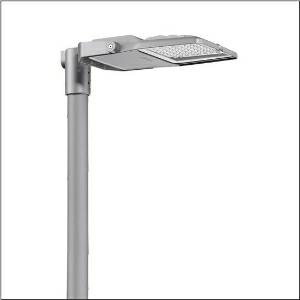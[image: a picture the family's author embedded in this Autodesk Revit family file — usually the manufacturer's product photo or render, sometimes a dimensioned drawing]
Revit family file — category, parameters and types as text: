
# Revit family: floodlight_fl_21_mini___pl61_5xa7776c2c3a_9e20
name_source: partatom
category: Lighting Fixtures
units: mm (PartAtom-declared; Revit-internal decimal feet)

## family parameters
Cut with Voids When Loaded = No
Host = Face
Light Source = No
Part Type = Normal
Room Calculation Point = No
Round Connector Dimension = Use Diameter
Shared = No

## types (1)
- --- (1 x LED, 11960 lm, 89 W, 3000K)
    Apparent Load = 89 VA
    CIE Flux Codes = 33 65 98 100 100
    Color Rendering = 70
    Color Temperature = 3000K
    Default Elevation = 1800 mm
    Description = Floodlight FL 21 mini, floodlight, primary light control with lens, of PMMA, primary optical cover: protective disc, of toughened safety glass, transparent, light distribution: PL61, light emission: direct distribution, installation type: surface-mounted, LED, High Power LED, rated luminous flux: 11.960lm, luminous efficacy: 134lm/W, light colour: 730, colour temperature: 3000K, control gear: ECG Smart Interface, control: flexible luminous flux parameterisation, time-dependent luminous flux control, constant luminous flux control, overheat protection, presetting dimming logarithmic, with terminal, 6-pole, mains connection: 220..240V, AC, 50/60Hz, start of lifetime: 89W, end of lifetime: 94W, reduction: 43W, luminaire housing, of diecast aluminium, powder-coated, Siteco® metallic grey (DB 702S), corrosivity category C5 according to DIN EN ISO 12944, mast bracket, of steel, galvanised, powder-coated, Siteco® metallic grey (DB 702S), protection rating (complete): IP66, insulation class (complete): insulation class II (safety insulation), certification: CE, protection symbol: D, impact resistance: IK08, permissible operating ambient temperature: -40..+40°C, permissible operating ambient temperature for outdoor applications: -40..+50°C, standard: DIN EN 12944, packaging unit: 1 piece

Light Distribution: PL61
    Height = 70 mm
    Lamp = 1 x LED
    Lamp Light Flux = 11960 lm
    Lamp Power = 89 W
    Lamp count = 1
    Length = 485 mm
    Luminous efficacy = 134 lm/W
    Manufacturer = Siteco
    ModVariant = No
    Model = 5XA7776C2C3A
    Number of Poles = 1
    OnlyDefault = Yes
    Power Factor = 1
    Product Name = Floodlight FL 21 mini | PL61
    Product group = floodlight | pylon top
    ProductGroupID = 6101
    Protection Class = Protection class II
    Protection Degree = IP 66
    RLX_Detail_Level = 1
    RlxData = <blob elided: 100693 chars, md5=29018446>
    Socket = socket
    Standby Power = 0 W
    System Light Flux = 11960 lm
    System Power = 89 W
    Type Comments = factory setting: luminous flux: 100 % | dim-lin: 254 | 456 mA
    Type Image = l_1007125.jpg
    URL = http://relux.com
    VarID = @adj_084391
    Voltage = 0 V
    Weight = 0.00 kg
    Width = 337 mm

## geometry (parser evidence)
native form markers: Blend x4, Sweep x13
no freeform markers — native parametric forms only
